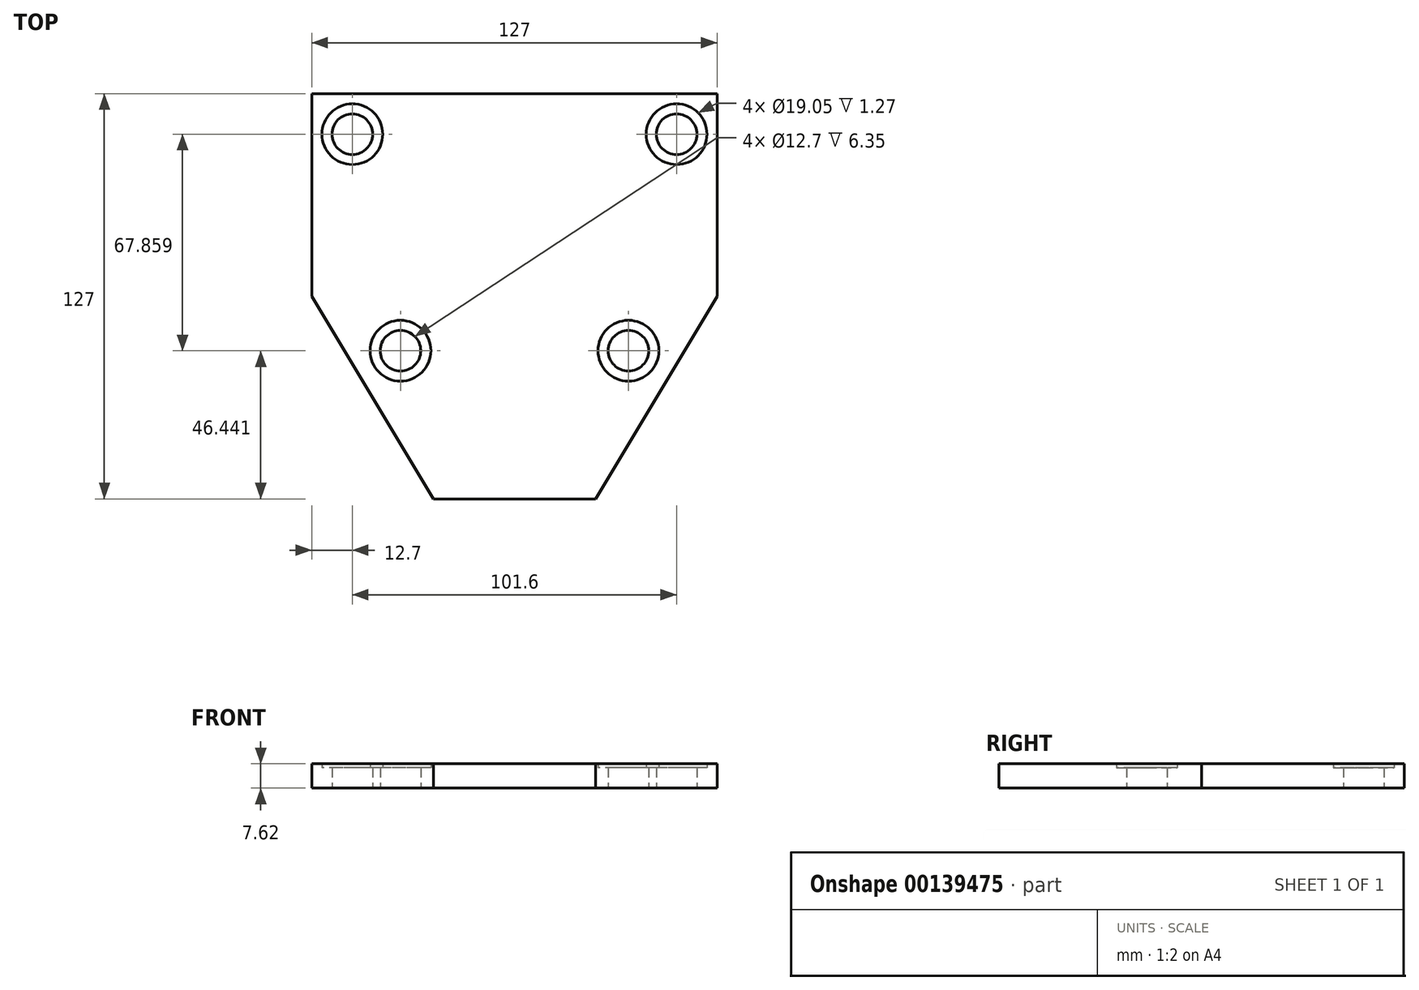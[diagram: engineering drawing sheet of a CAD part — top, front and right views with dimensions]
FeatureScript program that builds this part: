
annotation { "Feature Type Name" : "Feature", "Feature Type Description" : "" }
export const myFeature = defineFeature(function(context is Context, id is Id, definition is map)
    precondition{}
    {
        {
            var Q0;
            Q0=qCreatedBy(makeId("Top.planeOp"),FACE);
            var sketch = newSketch(context, id + "F0", { "sketchPlane" : qUnion([Q0])});
            skLineSegment(sketch, "E0", {"start": v(-25.4, -63.5) * mm, "end": v(25.4, -63.5) * mm});
            skLineSegment(sketch, "E1", {"start": v(25.4, -63.5) * mm, "end": v(63.5, 0) * mm});
            skLineSegment(sketch, "E2", {"start": v(63.5, 0) * mm, "end": v(63.5, 63.5) * mm});
            skLineSegment(sketch, "E3", {"start": v(63.5, 63.5) * mm, "end": v(-63.5, 63.5) * mm});
            skLineSegment(sketch, "E4", {"start": v(-63.5, 63.5) * mm, "end": v(-63.5, 0) * mm});
            skLineSegment(sketch, "E5", {"start": v(-63.5, 0) * mm, "end": v(-25.4, -63.5) * mm});
            skCircle(sketch, "E6", {"center": v(-50.8, 50.8) * mm, "radius": 6.35 * mm});
            skCircle(sketch, "E7", {"center": v(50.8, 50.8) * mm, "radius": 6.35 * mm});
            skCircle(sketch, "E8", {"center": v(35.72, -17.06) * mm, "radius": 6.35 * mm});
            skCircle(sketch, "E9", {"center": v(-35.72, -17.06) * mm, "radius": 6.35 * mm});
            skCircle(sketch, "E10", {"center": v(-50.8, 50.8) * mm, "radius": 9.53 * mm});
            skCircle(sketch, "E11", {"center": v(-35.72, -17.06) * mm, "radius": 9.53 * mm});
            skCircle(sketch, "E12", {"center": v(35.72, -17.06) * mm, "radius": 9.53 * mm});
            skCircle(sketch, "E13", {"center": v(50.8, 50.8) * mm, "radius": 9.53 * mm});
            skLineSegment(sketch, "E14", {"start": v(0, 63.5) * mm, "end": v(0, -63.5) * mm, "construction": true});
            skLineSegment(sketch, "E15", {"start": v(63.5, 0) * mm, "end": v(-63.5, 0) * mm, "construction": true});
            skPoint(sketch, "E16", {"position": v(0, 0) * mm});
            skSolve(sketch);
        }
        {
            var Q0;
            Q0=qCreatedBy(makeId("Top.planeOp"),FACE);
            var sketch = newSketch(context, id + "F1", { "sketchPlane" : qUnion([Q0])});
            skSolve(sketch);
        }
        {
            var Q0;
            Q0=qSketchRegion(id+"F1",true);
            var Q1;
            Q1=makeQuery(id+"F0.imprint","IMPRINT",FACE,{"disambiguationData":[TD([[makeQuery(id+"F0.imprint","IMPRINT",EDGE,{"derivedFrom":sQuery(id+"F0.wireOp",EDGE,"E0")}),1.0]])]});
            extrude(context, id + "F2", {"entities" : qUnion([Q0, Q1]), "depth" : 7.62 * mm});
        }
        {
            var Q0;
            Q0=makeQuery(id+"F0.imprint","IMPRINT",FACE,{"disambiguationData":[TD([[makeQuery(id+"F0.imprint","IMPRINT",EDGE,{"derivedFrom":sQuery(id+"F0.wireOp",EDGE,"E6")}),-1.0]])]});
            var Q1;
            Q1=makeQuery(id+"F0.imprint","IMPRINT",FACE,{"disambiguationData":[TD([[makeQuery(id+"F0.imprint","IMPRINT",EDGE,{"derivedFrom":sQuery(id+"F0.wireOp",EDGE,"E7")}),-1.0]])]});
            var Q2;
            Q2=makeQuery(id+"F0.imprint","IMPRINT",FACE,{"disambiguationData":[TD([[makeQuery(id+"F0.imprint","IMPRINT",EDGE,{"derivedFrom":sQuery(id+"F0.wireOp",EDGE,"E8")}),-1.0]])]});
            var Q3;
            Q3=makeQuery(id+"F0.imprint","IMPRINT",FACE,{"disambiguationData":[TD([[makeQuery(id+"F0.imprint","IMPRINT",EDGE,{"derivedFrom":sQuery(id+"F0.wireOp",EDGE,"E9")}),-1.0]])]});
            extrude(context, id + "F3", {"entities" : qUnion([Q0, Q1, Q2, Q3]), "operationType" : NewBodyOperationType.ADD, "depth" : 6.35 * mm});
        }
    });
